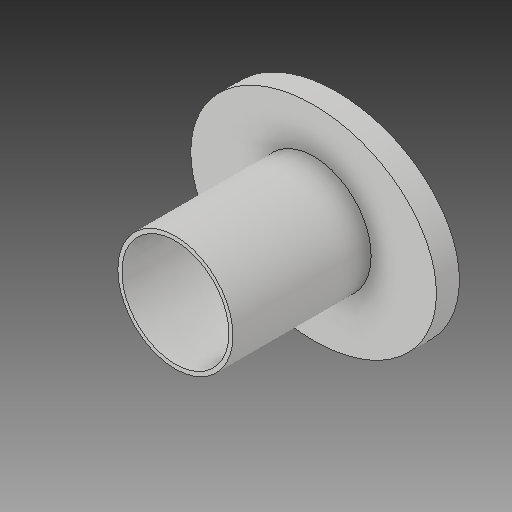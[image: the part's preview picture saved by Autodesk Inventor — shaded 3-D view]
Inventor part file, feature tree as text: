
AUTODESK INVENTOR PART (.ipt)
format: ipt  version: 2017 (Build 210142000, 142)  size: 118,784 bytes
history: native  units: mm
features: sketch x4, other x3
ambient origin geometry x8: Origin, YZ Plane, XZ Plane, XY Plane, X Axis, Y Axis, Z Axis, Center Point
bodies: Solid1 (feature_tree)
feature tree (7):
  other  "Pushfit-adapter-cap.ipt"
  other  "Solid1::Pushfit-adapter-cap.ipt"
  other  "TaggingFeature1"
  sketch  "Sketch1"  dims[d0=10.0mm]
  sketch  "Sketch2"
  sketch  "Sketch3"
  sketch  "Sketch4"
